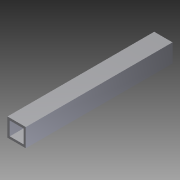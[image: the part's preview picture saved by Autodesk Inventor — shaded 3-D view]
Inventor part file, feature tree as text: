
AUTODESK INVENTOR PART (.ipt)
format: ipt  version: 2012 (Build 160160000, 160)  size: 74,240 bytes
history: native  units: in
note: dims shown in document units (in); Inventor stores cm internally (conversion verified against a paired STEP export)
features: extrude x1, shell x1, sketch x1
ambient origin geometry x8: Origin, YZ Plane, XZ Plane, XY Plane, X Axis, Y Axis, Z Axis, Center Point
bodies: Solid1 (feature_tree)
feature tree (3):
  extrude  "Extrusion1"  Depth=1.0in
  shell  "Shell1"  Thickness=8.0in
  sketch  "Sketch1"  dims[d0=1.0in d1=1.0in d2=8.0in d3=0.0in d4=0.125in]
